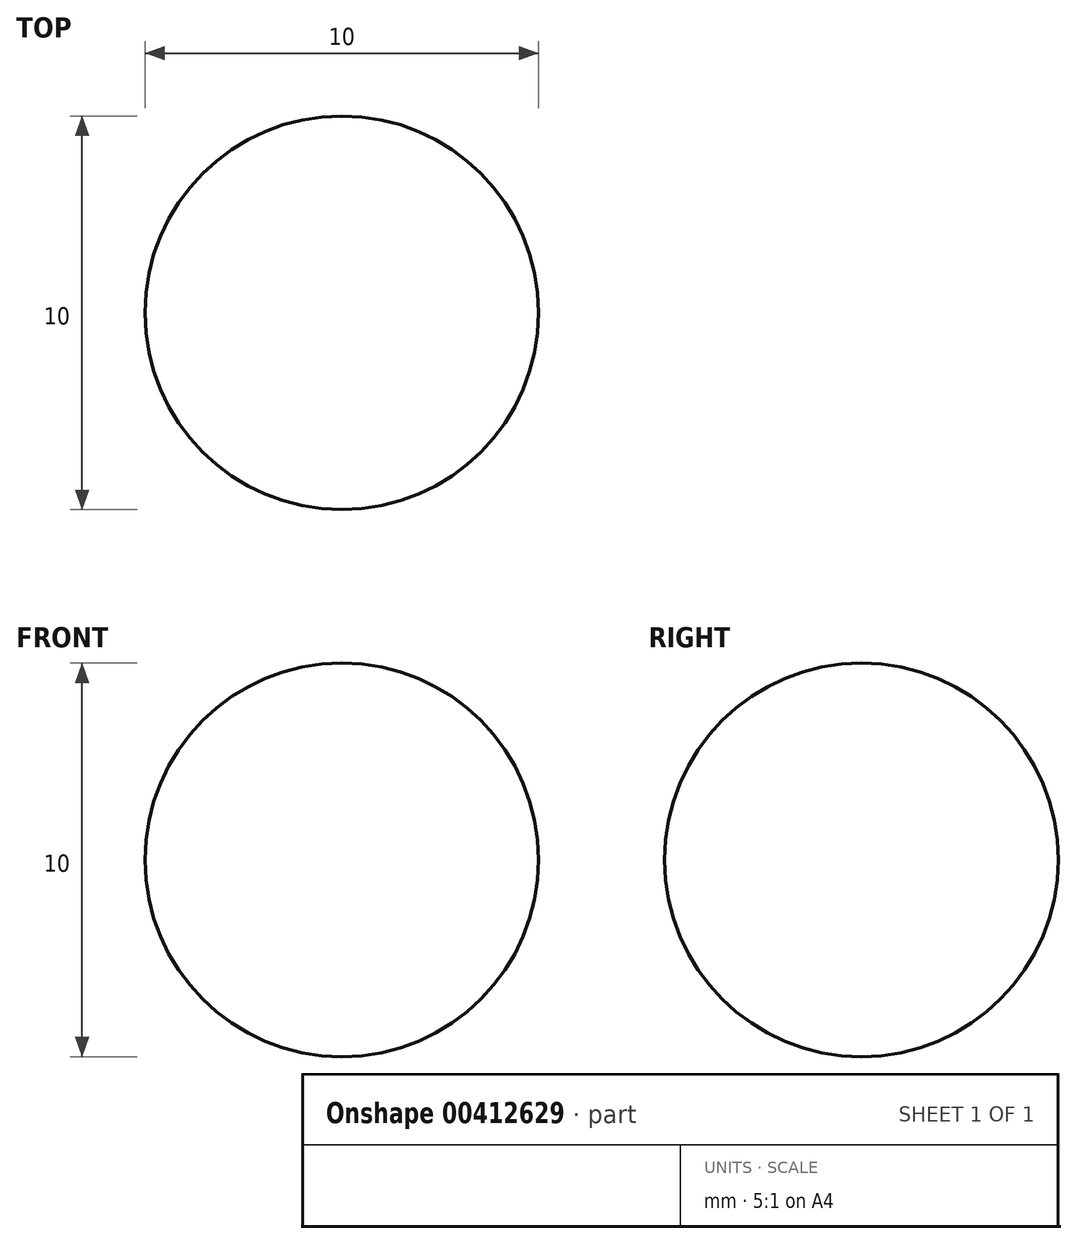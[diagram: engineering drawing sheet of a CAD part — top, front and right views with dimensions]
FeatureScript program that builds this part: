
annotation { "Feature Type Name" : "Feature", "Feature Type Description" : "" }
export const myFeature = defineFeature(function(context is Context, id is Id, definition is map)
    precondition{}
    {
        {
            var Q0;
            Q0=qCreatedBy(makeId("Front.planeOp"),FACE);
            var sketch = newSketch(context, id + "F0", { "sketchPlane" : qUnion([Q0])});
            skArc(sketch, "E0", {"start": v(0, 5) * mm, "mid": v(5, 0) * mm, "end": v(0, -5) * mm});
            skLineSegment(sketch, "E1", {"start": v(0, 5) * mm, "end": v(0, 0) * mm});
            skLineSegment(sketch, "E2", {"start": v(0, 0) * mm, "end": v(0, -5) * mm});
            skSolve(sketch);
        }
        {
            var Q0;
            Q0 = qSketchRegion(id + "F0", true);
            var Q1;
            Q1=sQuery(id+"F0.wireOp",EDGE,"E1");
            revolve(context, id + "F1", {"entities" : qUnion([Q0]), "axis" : qUnion([Q1]), "revolveType" : RevolveType.FULL});
        }
    });
